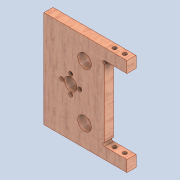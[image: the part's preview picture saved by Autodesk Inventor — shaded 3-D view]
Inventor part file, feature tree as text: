
AUTODESK INVENTOR PART (.ipt)
format: ipt  version: 2020 (Build 240168000, 168)  size: 195,072 bytes
history: native  units: mm
features: sketch x6, extrude x5, other x2, hole x1, reference x1
ambient origin geometry x8: Origin, YZ Plane, XZ Plane, XY Plane, X Axis, Y Axis, Z Axis, Center Point
bodies: Solid1 (feature_tree)
feature tree (15):
  extrude  "Extrusion1"  Depth=86.0mm
  extrude  "Extrusion4"  Depth=20.0mm
  extrude  "Extrusion5"  Depth=10.0mm TaperAngle=0.0deg
  extrude  "Extrusion6"  Depth=10.0mm TaperAngle=0.0deg
  hole  "Hole1"  [1 undecoded]
  extrude  "Extrusion7"  Depth=10.0mm TaperAngle=0.0deg
  sketch  "Sketch1"  dims[d0=73.5mm d1=86.0mm]
  sketch  "Sketch4"  dims[d2=8.0mm d3=0.0mm d19=20.0mm]
  sketch  "Sketch5"  dims[d20=66.0mm d21=10.0mm d22=0.0mm]
  reference  "Reference1"
  sketch  "Sketch6"  dims[d23=12.0mm d29=10.0mm d30=0.0mm]
  sketch  "Sketch7"  dims[d37=37.5mm d38=19.0mm]
  sketch  "Sketch8"  dims[d39=19.0mm d40=10.0mm d41=0.0mm d42=3.5mm d43=11.0mm d44=23.751158mm d46=22.0mm d47=16.0mm d48=9.0mm d49=6.0mm d50=3.5mm d51=6.0mm d52=4.0mm d53=2.0mm d54=90.0deg d55=8.0mm d56=20.594885mm d57=3.0mm d58=3.0mm d59=0.0mm d60=0.0mm]
  other  "0005-10-04 Y axis and extruder.iam"
  other  "0005-10-009.ipt:14"
note: 1 required parameter value undecoded (feature->parameter linkage not recoverable at this tier; creation-order binding heuristic only, values carry confidence <= 0.55)
